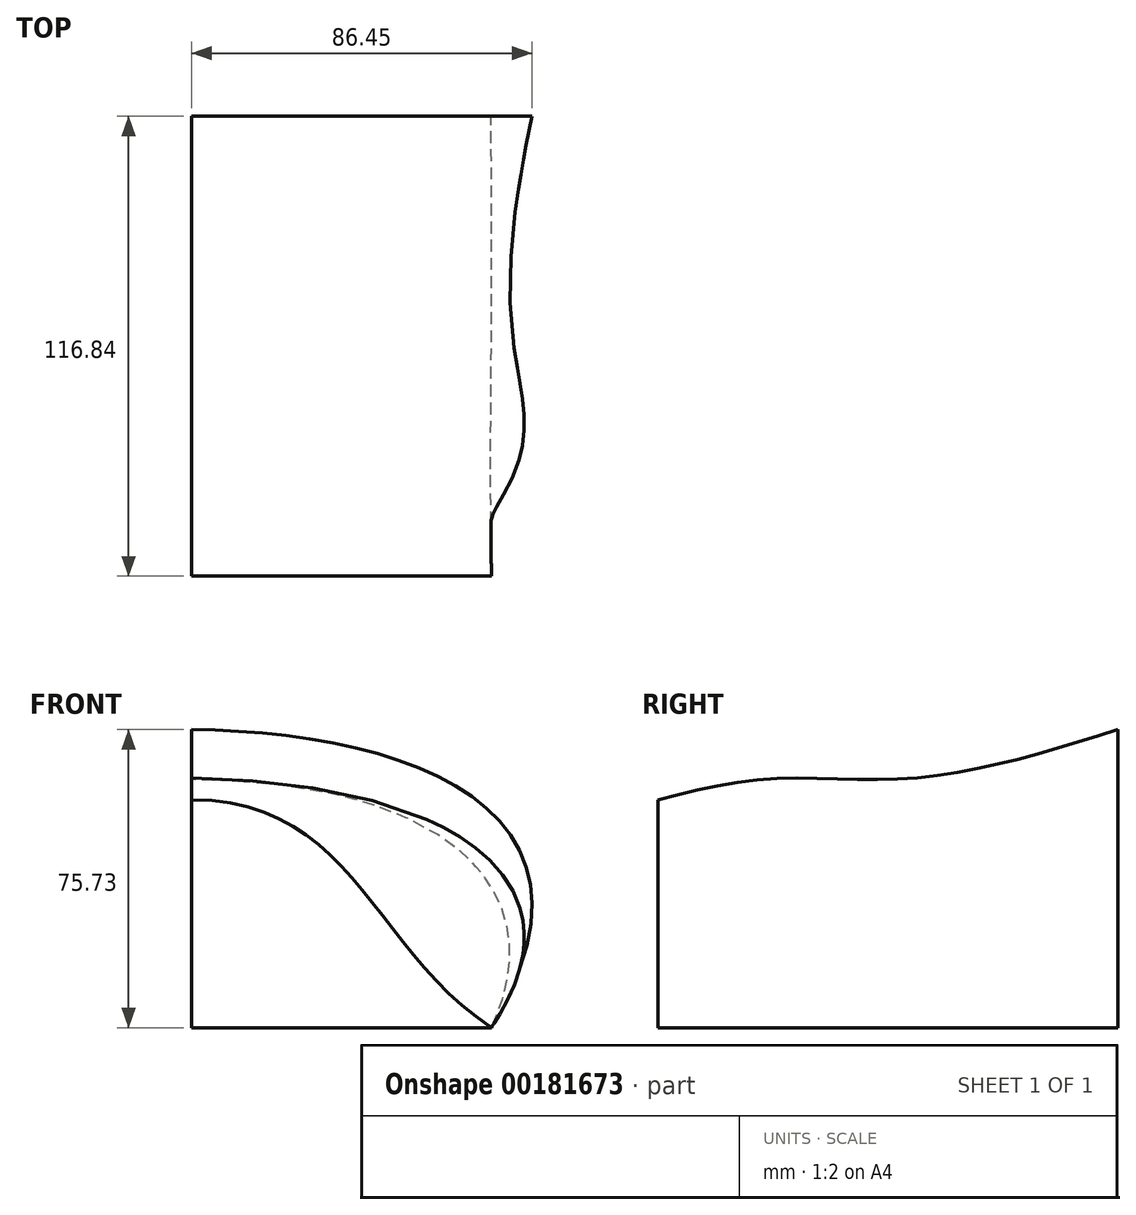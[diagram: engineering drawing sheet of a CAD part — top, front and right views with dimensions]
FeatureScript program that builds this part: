
annotation { "Feature Type Name" : "Feature", "Feature Type Description" : "" }
export const myFeature = defineFeature(function(context is Context, id is Id, definition is map)
    precondition{}
    {
        {
            var Q0;
            Q0=qCreatedBy(makeId("Front.planeOp"),FACE);
            var sketch = newSketch(context, id + "F0", { "sketchPlane" : qUnion([Q0])});
            skLineSegment(sketch, "E0", {"start": v(0, 0) * mm, "end": v(76.07, 0) * mm});
            skLineSegment(sketch, "E1", {"start": v(0, -10.42) * mm, "end": v(0, 75.73) * mm});
            skFitSpline(sketch, "E2", {"points": [v(0, 75.73) * mm, v(76.07, 0) * mm], "startDerivative": vector(148.67, -1.3) * mm, "endDerivative": vector(-105.64, -176.06) * mm});
            skSolve(sketch);
        }
        {
            var Q0;
            Q0=qCreatedBy(makeId("Front.planeOp"),FACE);
            cPlane(context, id + "F1", {"entities" : qUnion([Q0]), "cplaneType" : CPlaneType.OFFSET, "offset" : 91.44 * mm, "width" : 152.4 * mm, "height" : 152.4 * mm});
        }
        {
            var Q0;
            Q0=qCreatedBy(id+"F1.planeOp",FACE);
            var sketch = newSketch(context, id + "F2", { "sketchPlane" : qUnion([Q0])});
            skLineSegment(sketch, "E3", {"start": v(0, 0) * mm, "end": v(0, 62.97) * mm});
            skLineSegment(sketch, "E4", {"start": v(0, 0) * mm, "end": v(75.97, 0) * mm});
            skFitSpline(sketch, "E5", {"points": [v(0, 62.97) * mm, v(75.97, 0) * mm], "startDerivative": vector(196.18, -2.9) * mm, "endDerivative": vector(-57.2, -103.67) * mm});
            skSolve(sketch);
        }
        {
            var Q0;
            Q0=qCreatedBy(id+"F1.planeOp",FACE);
            cPlane(context, id + "F3", {"entities" : qUnion([Q0]), "cplaneType" : CPlaneType.OFFSET, "offset" : 25.4 * mm, "width" : 152.4 * mm, "height" : 152.4 * mm});
        }
        {
            var Q0;
            Q0=qCreatedBy(id+"F3.planeOp",FACE);
            var sketch = newSketch(context, id + "F4", { "sketchPlane" : qUnion([Q0])});
            skLineSegment(sketch, "E6", {"start": v(0, 0) * mm, "end": v(76.16, 0) * mm});
            skLineSegment(sketch, "E7", {"start": v(0, 0) * mm, "end": v(0, 57.91) * mm});
            skFitSpline(sketch, "E8", {"points": [v(0, 57.91) * mm, v(76.16, 0) * mm], "startDerivative": vector(123.58, -0.52) * mm, "endDerivative": vector(91.91, -61.06) * mm});
            skSolve(sketch);
        }
        {
            var Q0;
            Q0=qCreatedBy(id+"F1.planeOp",FACE);
            cPlane(context, id + "F5", {"entities" : qUnion([Q0]), "cplaneType" : CPlaneType.OFFSET, "offset" : 35.56 * mm, "oppositeDirection" : true, "width" : 152.4 * mm, "height" : 152.4 * mm});
        }
        {
            var Q0;
            Q0=qCreatedBy(id+"F5.planeOp",FACE);
            var sketch = newSketch(context, id + "F6", { "sketchPlane" : qUnion([Q0])});
            skLineSegment(sketch, "E9", {"start": v(0, 0) * mm, "end": v(0, 63.17) * mm});
            skLineSegment(sketch, "E10", {"start": v(0, 0) * mm, "end": v(76.14, 0) * mm});
            skFitSpline(sketch, "E11", {"points": [v(0, 63.17) * mm, v(76.14, 0) * mm], "startDerivative": vector(183.26, -1.14) * mm, "endDerivative": vector(-57.9, -110.2) * mm});
            skSolve(sketch);
        }
        {
            var Q0;
            Q0=makeQuery(id+"F4.imprint","IMPRINT",FACE,{"disambiguationData":[TD([[makeQuery(id+"F4.imprint","IMPRINT",EDGE,{"derivedFrom":sQuery(id+"F4.wireOp",EDGE,"E6")}),1.0]])]});
            var Q1;
            Q1=makeQuery(id+"F2.imprint","IMPRINT",FACE,{"disambiguationData":[TD([[makeQuery(id+"F2.imprint","IMPRINT",EDGE,{"derivedFrom":sQuery(id+"F2.wireOp",EDGE,"E3")}),-1.0]])]});
            var Q2;
            Q2=makeQuery(id+"F6.imprint","IMPRINT",FACE,{"disambiguationData":[TD([[makeQuery(id+"F6.imprint","IMPRINT",EDGE,{"derivedFrom":sQuery(id+"F6.wireOp",EDGE,"E9")}),-1.0]])]});
            var Q3;
            {var subQ0=sQuery(id+"F0.wireOp",EDGE,"E0");Q3=makeQuery(id+"F0.imprint","IMPRINT",FACE,{"disambiguationData":[TD([[makeQuery(id+"F0.imprint","IMPRINT",EDGE,{"derivedFrom":subQ0}),1.0]])]});}
            loft(context, id + "F7", {"sheetProfilesArray" : [{ "sheetProfileEntities" : qUnion([Q0]) }, { "sheetProfileEntities" : qUnion([Q1]) }, { "sheetProfileEntities" : qUnion([Q2]) }, { "sheetProfileEntities" : qUnion([Q3]) }]});
        }
    });
